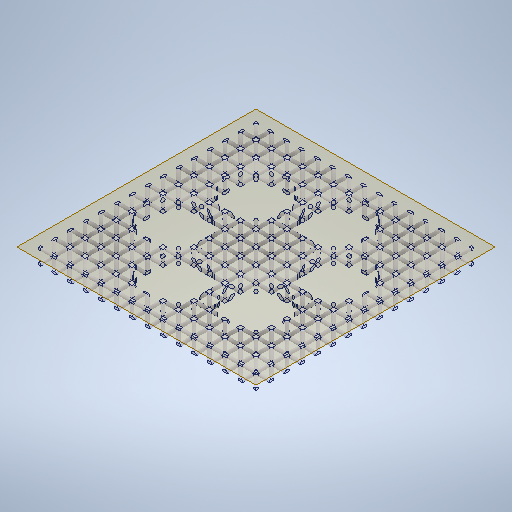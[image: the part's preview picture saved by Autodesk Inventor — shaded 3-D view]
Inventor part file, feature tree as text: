
AUTODESK INVENTOR PART (.ipt)
format: ipt  version: 2025.3 (Build 293356000, 356)  size: 3,807,232 bytes
history: native  units: in
note: dims shown in document units (in); Inventor stores cm internally (conversion verified against a paired STEP export)
features: projected_geometry x2, pattern_linear x1, plane x1, extrude x1, sketch x1, other x1
ambient origin geometry x8: Origin, YZ Plane, XZ Plane, XY Plane, X Axis, Y Axis, Z Axis, Center Point
bodies: Solid1 (feature_tree)
feature tree (7):
  pattern_linear  "Rectangular Pattern1"  Count1=14 Spacing1=0.315in
  plane  "Work Plane1"
  extrude  "Extrusion1"  Depth=2.3622in
  sketch  "Sketch1"  dims[d6=4.3307in d7=2.3622in d8=1.1811in d9=1.1811in d10=1.1811in d11=1.1811in d12=1.1811in d13=1.1811in d14=4.3307in d15=0.0in]
  other  "Cut-Extrude14"
  projected_geometry  "Project Cut Edges1"
  projected_geometry  "Project Cut Edges2"
